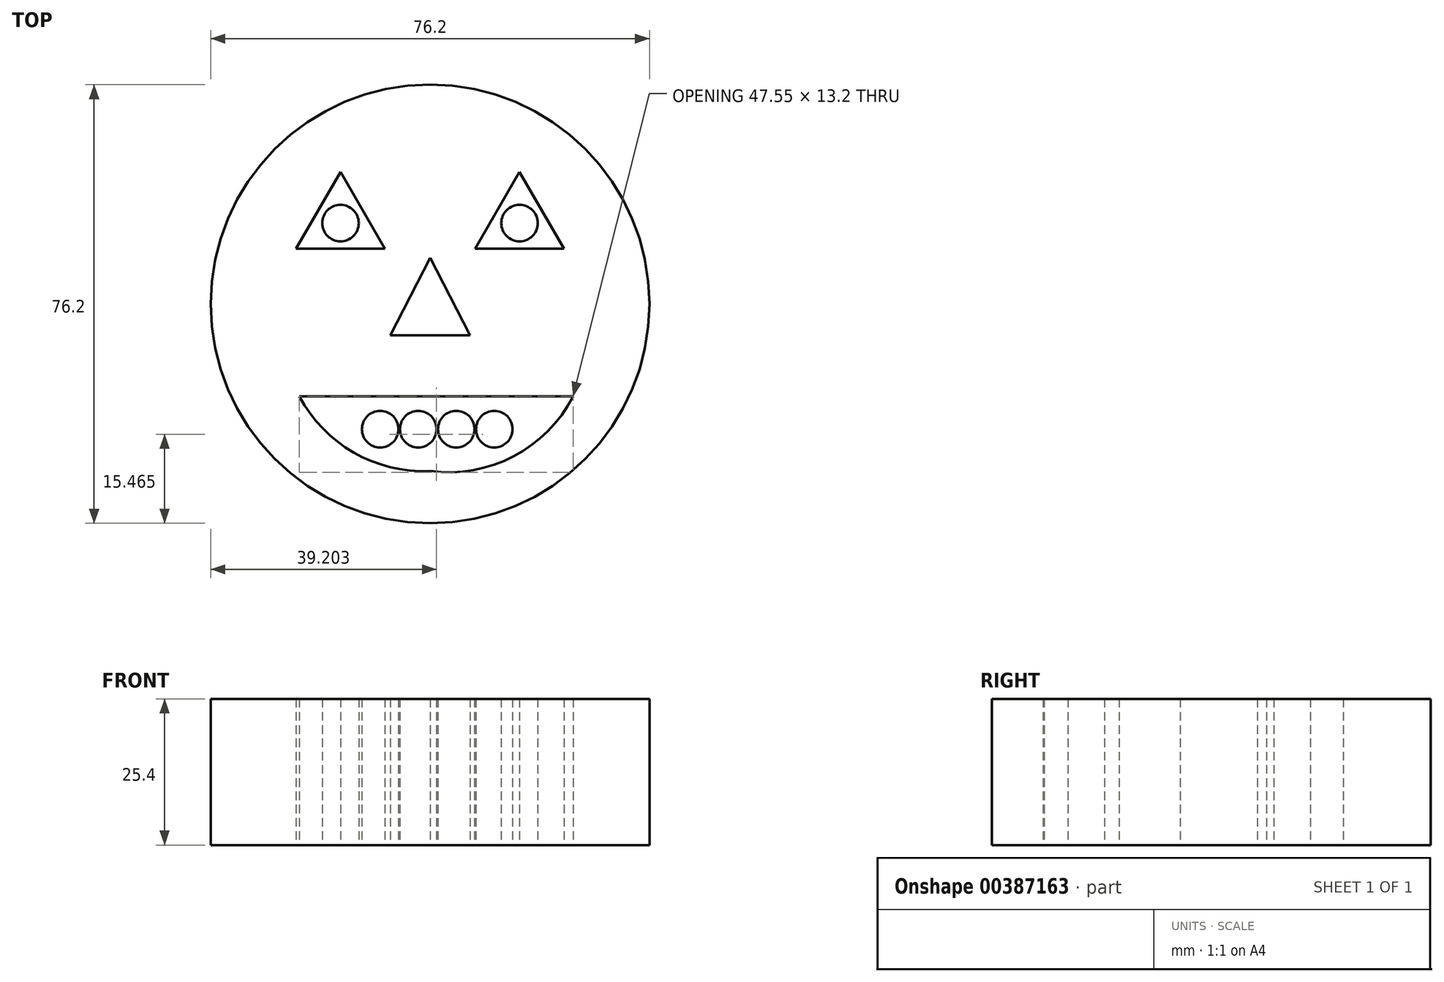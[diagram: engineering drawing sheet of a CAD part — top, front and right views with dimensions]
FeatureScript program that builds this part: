
annotation { "Feature Type Name" : "Feature", "Feature Type Description" : "" }
export const myFeature = defineFeature(function(context is Context, id is Id, definition is map)
    precondition{}
    {
        {
            var Q0;
            Q0=qCreatedBy(makeId("Top.planeOp"),FACE);
            var sketch = newSketch(context, id + "F0", { "sketchPlane" : qUnion([Q0])});
            skCircle(sketch, "E0", {"center": v(-0.39, 2.28) * mm, "radius": 38.1 * mm});
            skCircle(sketch, "E1", {"center": v(-15.94, 16.33) * mm, "radius": 3.18 * mm});
            skCircle(sketch, "E2", {"center": v(15.16, 16.33) * mm, "radius": 3.18 * mm});
            skCircle(sketch, "E3", {"center": v(-9.04, -19.47) * mm, "radius": 3.18 * mm});
            skCircle(sketch, "E4", {"center": v(-2.43, -19.47) * mm, "radius": 3.18 * mm});
            skCircle(sketch, "E5", {"center": v(4.17, -19.47) * mm, "radius": 3.18 * mm});
            skCircle(sketch, "E6", {"center": v(10.77, -19.47) * mm, "radius": 3.18 * mm});
            skLineSegment(sketch, "E7", {"start": v(-0.39, 10.28) * mm, "end": v(-7.3, -3.14) * mm});
            skLineSegment(sketch, "E8", {"start": v(-7.3, -3.14) * mm, "end": v(6.53, -3.14) * mm});
            skLineSegment(sketch, "E9", {"start": v(6.53, -3.14) * mm, "end": v(-0.39, 10.28) * mm});
            skLineSegment(sketch, "E10", {"start": v(-15.94, 25.22) * mm, "end": v(-23.63, 11.88) * mm});
            skLineSegment(sketch, "E11", {"start": v(-23.63, 11.88) * mm, "end": v(-8.24, 11.88) * mm});
            skLineSegment(sketch, "E12", {"start": v(-8.24, 11.88) * mm, "end": v(-15.94, 25.22) * mm});
            skLineSegment(sketch, "E13", {"start": v(15.16, 25.22) * mm, "end": v(22.86, 11.88) * mm});
            skLineSegment(sketch, "E14", {"start": v(22.86, 11.88) * mm, "end": v(7.47, 11.88) * mm});
            skLineSegment(sketch, "E15", {"start": v(7.47, 11.88) * mm, "end": v(15.16, 25.22) * mm});
            skArc(sketch, "E16", {"start": v(-23.06, -13.75) * mm, "mid": v(-13.61, -23.55) * mm, "end": v(-0.39, -26.75) * mm});
            skArc(sketch, "E17", {"start": v(-0.39, -26.75) * mm, "mid": v(14.1, -24.2) * mm, "end": v(24.49, -13.75) * mm});
            skLineSegment(sketch, "E18", {"start": v(-23.06, -13.75) * mm, "end": v(24.49, -13.75) * mm});
            skSolve(sketch);
        }
        {
            var Q0;
            Q0=makeQuery(id+"F0.imprint","IMPRINT",FACE,{"disambiguationData":[TD([[makeQuery(id+"F0.imprint","IMPRINT",EDGE,{"derivedFrom":sQuery(id+"F0.wireOp",EDGE,"E0")}),1.0]])]});
            extrude(context, id + "F1", {"entities" : qUnion([Q0]), "depth" : 25.4 * mm});
        }
        {
            var Q0;
            Q0=makeQuery(id+"F0.imprint","IMPRINT",FACE,{"disambiguationData":[TD([[makeQuery(id+"F0.imprint","IMPRINT",EDGE,{"derivedFrom":sQuery(id+"F0.wireOp",EDGE,"E1")}),1.0]])]});
            extrude(context, id + "F2", {"entities" : qUnion([Q0]), "depth" : 25.4 * mm});
        }
        {
            var Q0;
            Q0=makeQuery(id+"F0.imprint","IMPRINT",FACE,{"disambiguationData":[TD([[makeQuery(id+"F0.imprint","IMPRINT",EDGE,{"derivedFrom":sQuery(id+"F0.wireOp",EDGE,"E2")}),-1.0]])]});
            extrude(context, id + "F3", {"entities" : qUnion([Q0]), "depth" : 25.4 * mm});
        }
        {
            var Q0;
            Q0=makeQuery(id+"F0.imprint","IMPRINT",FACE,{"disambiguationData":[TD([[makeQuery(id+"F0.imprint","IMPRINT",EDGE,{"derivedFrom":sQuery(id+"F0.wireOp",EDGE,"E3")}),-1.0]])]});
            extrude(context, id + "F4", {"entities" : qUnion([Q0]), "depth" : 25.4 * mm});
        }
    });
